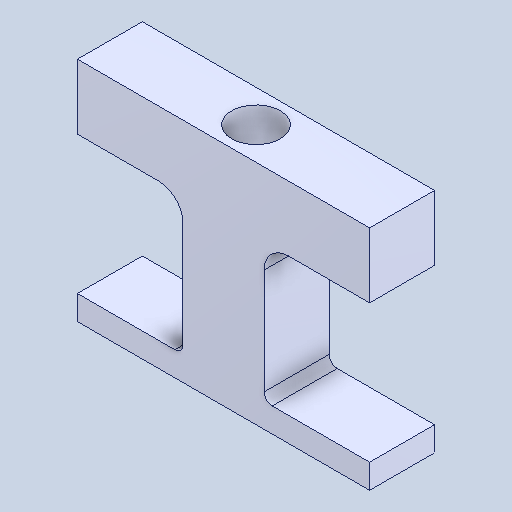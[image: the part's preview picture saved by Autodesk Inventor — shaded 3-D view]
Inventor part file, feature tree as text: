
AUTODESK INVENTOR PART (.ipt)
format: ipt  version: 2022 (Build 260153000, 153)  size: 124,928 bytes
history: mixed  units: in
note: dims shown in document units (in); Inventor stores cm internally (conversion verified against a paired STEP export)
features: fillet x1, imported_body x1
ambient origin geometry x8: Origin, YZ Plane, XZ Plane, XY Plane, X Axis, Y Axis, Z Axis, Center Point
bodies: Solid1 (imported_parasolid)
feature tree (2):
  fillet  "Fillet2"  [1 undecoded]
  imported_body  NMx_Import_Brep_tag  [imported B-rep: ~21 faces, bbox_mm=[36.0, 28.0, 8.0]]
note: 1 required parameter value undecoded (feature->parameter linkage not recoverable at this tier; creation-order binding heuristic only, values carry confidence <= 0.55)
